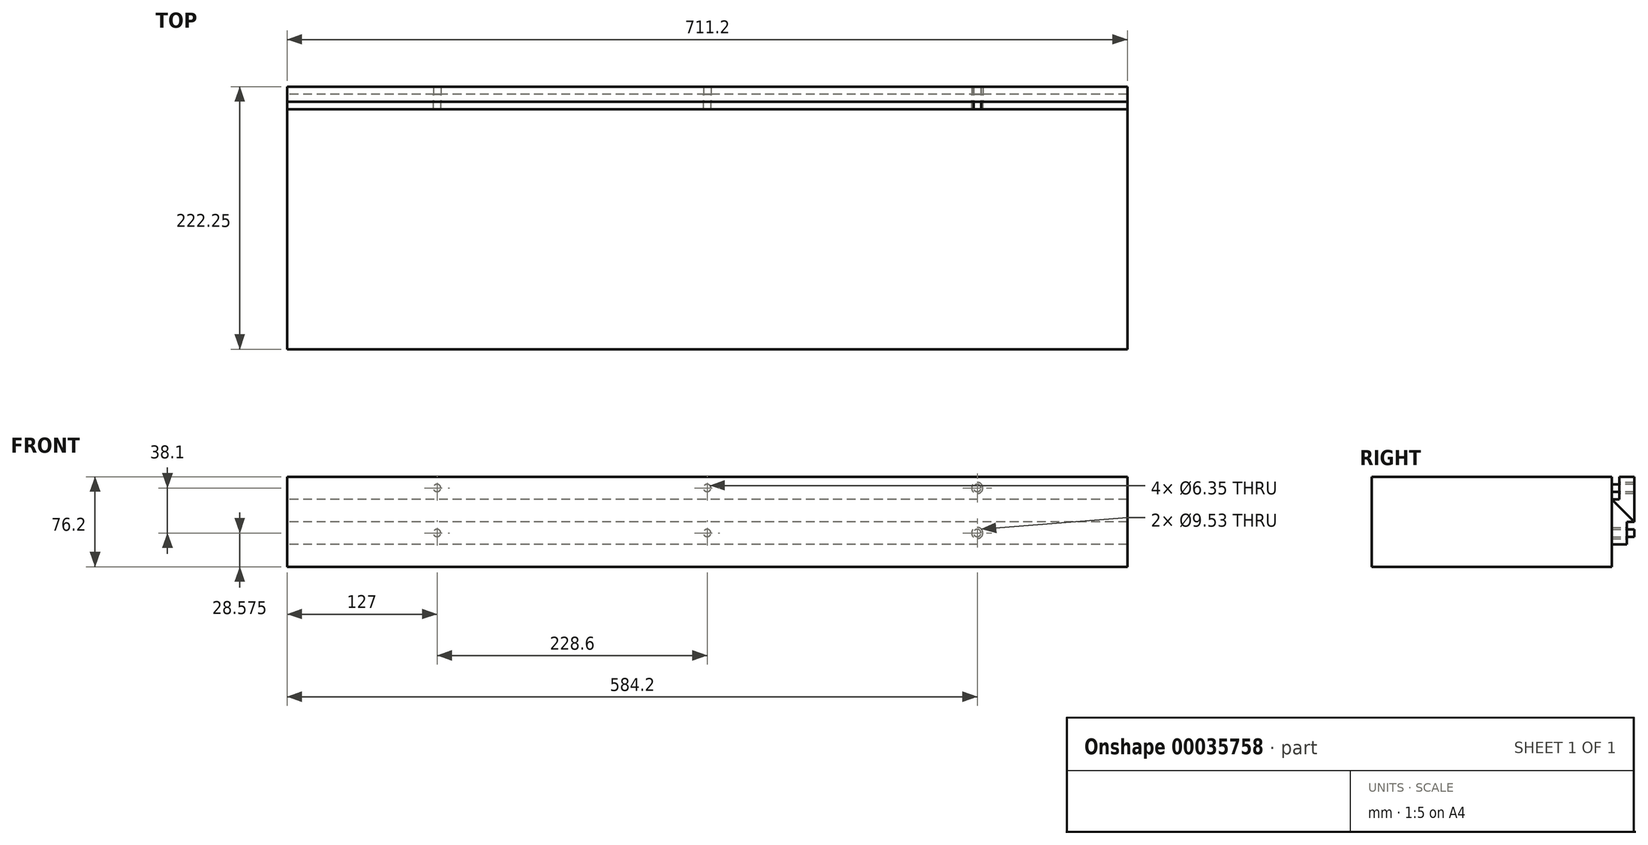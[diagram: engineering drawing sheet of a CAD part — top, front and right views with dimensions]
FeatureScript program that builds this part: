
annotation { "Feature Type Name" : "Feature", "Feature Type Description" : "" }
export const myFeature = defineFeature(function(context is Context, id is Id, definition is map)
    precondition{}
    {
        {
            var Q0;
            Q0=qCreatedBy(makeId("Right.planeOp"),FACE);
            var sketch = newSketch(context, id + "F0", { "sketchPlane" : qUnion([Q0])});
            skLineSegment(sketch, "E0.bottom", {"start": v(-101.6, 38.1) * mm, "end": v(101.6, 38.1) * mm});
            skLineSegment(sketch, "E0.top", {"start": v(-101.6, -38.1) * mm, "end": v(101.6, -38.1) * mm});
            skLineSegment(sketch, "E0.left", {"start": v(-101.6, 38.1) * mm, "end": v(-101.6, -38.1) * mm});
            skLineSegment(sketch, "E0.right", {"start": v(101.6, 38.1) * mm, "end": v(101.6, -38.1) * mm});
            skLineSegment(sketch, "E1", {"start": v(-101.6, 38.1) * mm, "end": v(101.6, -38.1) * mm, "construction": true});
            skPoint(sketch, "E2", {"position": v(0, 0) * mm});
            skSolve(sketch);
        }
        {
            var Q0;
            Q0 = qSketchRegion(id + "F0", true);
            extrude(context, id + "F1", {"entities" : qUnion([Q0]), "endBound" : BoundingType.SYMMETRIC, "depth" : 711.2 * mm});
        }
        {
            var Q0;
            Q0=qCreatedBy(makeId("Right.planeOp"),FACE);
            var sketch = newSketch(context, id + "F2", { "sketchPlane" : qUnion([Q0])});
            skLineSegment(sketch, "E3", {"start": v(120.65, 0) * mm, "end": v(120.65, 38.1) * mm});
            skLineSegment(sketch, "E4", {"start": v(101.6, 38.1) * mm, "end": v(120.65, 38.1) * mm});
            skLineSegment(sketch, "E5", {"start": v(101.6, 38.1) * mm, "end": v(101.6, 0) * mm});
            skPoint(sketch, "E6.orphan", {"position": v(120.65, -38.1) * mm});
            skLineSegment(sketch, "E7", {"start": v(101.6, 0) * mm, "end": v(120.65, 0) * mm});
            skLineSegment(sketch, "E8", {"start": v(101.6, 19.05) * mm, "end": v(120.65, 0) * mm});
            skSolve(sketch);
        }
        {
            var Q0;
            {var subQ1=sQuery(id+"F2.wireOp",EDGE,"E4");Q0=makeQuery(id+"F2.imprint","IMPRINT",FACE,{"disambiguationData":[TD([[makeQuery(id+"F2.imprint","IMPRINT",EDGE,{"derivedFrom":subQ1}),-1.0]])]});}
            var Q1;
            {var subQ1=sQuery(id+"F2.wireOp",EDGE,"f3495305-2aaa-4ecc-9b9f-8efbbdf2ab74");Q1=makeQuery(id+"F2.imprint","IMPRINT",FACE,{"disambiguationData":[TD([[makeQuery(id+"F2.imprint","IMPRINT",EDGE,{"derivedFrom":subQ1}),1.0]])]});}
            var Q2;
            {var subQ1=sQuery(id+"F2.wireOp",EDGE,"f3495305-2aaa-4ecc-9b9f-8efbbdf2ab74");Q2=makeQuery(id+"F2.imprint","IMPRINT",FACE,{"disambiguationData":[TD([[makeQuery(id+"F2.imprint","IMPRINT",EDGE,{"derivedFrom":subQ1}),-1.0]])]});}
            extrude(context, id + "F3", {"entities" : qUnion([Q0, Q1, Q2]), "endBound" : BoundingType.SYMMETRIC, "depth" : 711.2 * mm});
        }
        {
            var Q0;
            Q0=makeQuery(id+"F3.opExtrude","SWEPT_BODY",BODY,{"disambiguationData":[OSD([sQuery(id+"F2.wireOp",EDGE,"05a05af1-1879-4c6c-b0c8-93491ac4f794.0"),sQuery(id+"F2.wireOp",EDGE,"E3"),sQuery(id+"F2.wireOp",EDGE,"E4"),sQuery(id+"F2.wireOp",EDGE,"86c9e914-bfff-420e-a051-b4136f603c3d")])]});
            transform(context, id + "F4", {"entities" : qUnion([Q0]), "transformType" : TransformType.TRANSLATION_3D, "dx" : 0 * mm, "dy" : 0 * mm, "dz" : 0 * mm, "makeCopy" : true});
        }
        {
            var Q0;
            Q0=makeQuery(id+"F4.opPattern","COPY",BODY,{"derivedFrom":makeQuery(id+"F3.opExtrude","SWEPT_BODY",BODY,{"disambiguationData":[OSD([sQuery(id+"F2.wireOp",EDGE,"05a05af1-1879-4c6c-b0c8-93491ac4f794.0"),sQuery(id+"F2.wireOp",EDGE,"E3"),sQuery(id+"F2.wireOp",EDGE,"E4"),sQuery(id+"F2.wireOp",EDGE,"86c9e914-bfff-420e-a051-b4136f603c3d")])]}),"instanceName":"1"});
            transform(context, id + "F5", {"entities" : qUnion([Q0]), "transformType" : TransformType.TRANSLATION_3D, "dx" : 0 * mm, "dy" : 38.24 * mm, "dz" : -39.85 * mm, "makeCopy" : false});
        }
        {
            var Q0;
            Q0=makeQuery(id+"F3.opExtrude","SWEPT_FACE",FACE,{"disambiguationData":[OSD([sQuery(id+"F2.wireOp",EDGE,"E5")])]});
            var sketch = newSketch(context, id + "F6", { "sketchPlane" : qUnion([Q0])});
            skLineSegment(sketch, "E9.0", {"start": v(-355.6, 38.1) * mm, "end": v(-355.6, 19.05) * mm, "construction": true});
            skLineSegment(sketch, "E10", {"start": v(-355.6, 28.58) * mm, "end": v(355.6, 28.58) * mm, "construction": true});
            skCircle(sketch, "E11", {"center": v(0, 28.58) * mm, "radius": 3.18 * mm});
            skCircle(sketch, "E12", {"center": v(-228.6, 28.57) * mm, "radius": 3.18 * mm});
            skCircle(sketch, "E13", {"center": v(0, 28.58) * mm, "radius": 4.76 * mm});
            skCircle(sketch, "E14", {"center": v(-228.6, 28.57) * mm, "radius": 4.76 * mm});
            skCircle(sketch, "E15.MirrorC", {"center": v(228.6, 28.57) * mm, "radius": 4.76 * mm});
            skCircle(sketch, "E16.MirrorC", {"center": v(228.6, 28.57) * mm, "radius": 3.18 * mm});
            skSolve(sketch);
        }
        {
            var Q0;
            Q0=makeQuery(id+"F6.imprint","IMPRINT",FACE,{"disambiguationData":[TD([[makeQuery(id+"F6.imprint","IMPRINT",EDGE,{"derivedFrom":sQuery(id+"F6.wireOp",EDGE,"E11")}),1.0]])]});
            var Q1;
            Q1=makeQuery(id+"F6.imprint","IMPRINT",FACE,{"disambiguationData":[TD([[makeQuery(id+"F6.imprint","IMPRINT",EDGE,{"derivedFrom":sQuery(id+"F6.wireOp",EDGE,"E12")}),1.0]])]});
            var Q2;
            Q2=makeQuery(id+"F6.imprint","IMPRINT",FACE,{"disambiguationData":[TD([[makeQuery(id+"F6.imprint","IMPRINT",EDGE,{"derivedFrom":sQuery(id+"F6.wireOp",EDGE,"E16.MirrorC")}),-1.0]])]});
            extrude(context, id + "F7", {"entities" : qUnion([Q0, Q1, Q2]), "operationType" : NewBodyOperationType.REMOVE, "endBound" : BoundingType.THROUGH_ALL, "oppositeDirection" : true, "depth" : 25.4 * mm});
        }
        {
            var Q0;
            Q0=makeQuery(id+"F6.imprint","IMPRINT",FACE,{"disambiguationData":[TD([[makeQuery(id+"F6.imprint","IMPRINT",EDGE,{"derivedFrom":sQuery(id+"F6.wireOp",EDGE,"E16.MirrorC")}),-1.0]])]});
            var Q1;
            Q1=makeQuery(id+"F6.imprint","IMPRINT",FACE,{"disambiguationData":[TD([[makeQuery(id+"F6.imprint","IMPRINT",EDGE,{"derivedFrom":sQuery(id+"F6.wireOp",EDGE,"E15.MirrorC")}),-1.0]])]});
            var Q2;
            Q2=makeQuery(id+"F6.imprint","IMPRINT",FACE,{"disambiguationData":[TD([[makeQuery(id+"F6.imprint","IMPRINT",EDGE,{"derivedFrom":sQuery(id+"F6.wireOp",EDGE,"E11")}),1.0]])]});
            var Q3;
            Q3=makeQuery(id+"F6.imprint","IMPRINT",FACE,{"disambiguationData":[TD([[makeQuery(id+"F6.imprint","IMPRINT",EDGE,{"derivedFrom":sQuery(id+"F6.wireOp",EDGE,"E12")}),1.0]])]});
            var Q4;
            Q4=makeQuery(id+"F6.imprint","IMPRINT",FACE,{"disambiguationData":[TD([[makeQuery(id+"F6.imprint","IMPRINT",EDGE,{"derivedFrom":sQuery(id+"F6.wireOp",EDGE,"E12")}),-1.0]])]});
            var Q5;
            Q5=makeQuery(id+"F6.imprint","IMPRINT",FACE,{"disambiguationData":[TD([[makeQuery(id+"F6.imprint","IMPRINT",EDGE,{"derivedFrom":sQuery(id+"F6.wireOp",EDGE,"E11")}),-1.0]])]});
            extrude(context, id + "F8", {"entities" : qUnion([Q0, Q1, Q2, Q3, Q4, Q5]), "operationType" : NewBodyOperationType.REMOVE, "oppositeDirection" : true, "depth" : 6.35 * mm});
        }
        {
            var Q0;
            Q0=makeQuery(id+"F4.opPattern","COPY",BODY,{"derivedFrom":makeQuery(id+"F3.opExtrude","SWEPT_BODY",BODY,{"disambiguationData":[OSD([sQuery(id+"F2.wireOp",EDGE,"E3"),sQuery(id+"F2.wireOp",EDGE,"E4"),sQuery(id+"F2.wireOp",EDGE,"E5"),sQuery(id+"F2.wireOp",EDGE,"E8")])]}),"instanceName":"1"});
            deleteBodies(context, id + "F9", {"entities" : qUnion([Q0])});
        }
        {
            var Q0;
            Q0=makeQuery(id+"F3.opExtrude","SWEPT_BODY",BODY,{"disambiguationData":[OSD([sQuery(id+"F2.wireOp",EDGE,"E3"),sQuery(id+"F2.wireOp",EDGE,"E4"),sQuery(id+"F2.wireOp",EDGE,"E5"),sQuery(id+"F2.wireOp",EDGE,"E8")])]});
            var Q1;
            Q1=makeQuery(id+"F3.opExtrude","SWEPT_EDGE",EDGE,{"disambiguationData":[OSD([sQuery(id+"F2.wireOp",EDGE,"E5"),sQuery(id+"F2.wireOp",EDGE,"E8")])]});
            transform(context, id + "F10", {"entities" : qUnion([Q0]), "transformType" : TransformType.ROTATION, "transformAxis" : qUnion([Q1]), "angle" : 180 * degree, "oppositeDirection" : true, "makeCopy" : true});
        }
        {
            var Q0;
            Q0=makeQuery(id+"F10.opPattern","COPY",BODY,{"derivedFrom":makeQuery(id+"F3.opExtrude","SWEPT_BODY",BODY,{"disambiguationData":[OSD([sQuery(id+"F2.wireOp",EDGE,"E3"),sQuery(id+"F2.wireOp",EDGE,"E4"),sQuery(id+"F2.wireOp",EDGE,"E5"),sQuery(id+"F2.wireOp",EDGE,"E8")])]}),"instanceName":"1"});
            transform(context, id + "F11", {"entities" : qUnion([Q0]), "transformType" : TransformType.TRANSLATION_3D, "dx" : 0 * mm, "dy" : 19.05 * mm, "dz" : -19.05 * mm, "makeCopy" : false});
        }
    });
